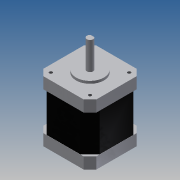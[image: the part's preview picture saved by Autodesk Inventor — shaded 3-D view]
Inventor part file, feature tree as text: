
AUTODESK INVENTOR PART (.ipt)
format: ipt  version: 2013 (Build 170138000, 138)  size: 163,840 bytes
history: native  units: mm
features: sketch x7, extrude x6, projected_geometry x3, pattern_circular x2, hole x1, chamfer x1
ambient origin geometry x8: Origin, YZ Plane, XZ Plane, XY Plane, X Axis, Y Axis, Z Axis, Center Point
bodies: Solid1 (feature_tree)
feature tree (20):
  extrude  "Extrusion1"  Depth=48.0mm TaperAngle=0.0deg
  extrude  "Extrusion2"  Depth=2.0mm TaperAngle=0.0deg
  extrude  "Extrusion3"  Depth=22.0mm TaperAngle=0.0deg
  extrude  "Extrusion4"  Depth=15.0mm TaperAngle=0.0deg
  hole  "Hole1"  [1 undecoded]
  chamfer  "Chamfer1"  Distance=30.0mm
  extrude  "Extrusion5"  Depth=40.0mm TaperAngle=360.0deg
  pattern_circular  "Circular Pattern1"  [2 undecoded]
  extrude  "Extrusion6"  Depth=40.0mm TaperAngle=360.0deg
  pattern_circular  "Circular Pattern2"  [2 undecoded]
  sketch  "Sketch1"  dims[d0=42.0mm d1=48.0mm d2=0.0mm]
  sketch  "Sketch2"  dims[d3=22.0mm d5=2.0mm d6=0.0mm]
  sketch  "Sketch3"  dims[d7=5.0mm d9=22.0mm d10=0.0mm]
  sketch  "Sketch4"  dims[d11=2.0mm d12=15.0mm d13=0.0mm]
  sketch  "Sketch5"  dims[d14=31.0mm]
  sketch  "Sketch6"  dims[d15=2.459mm d16=48.0mm d17=4.0mm d18=2.0mm d19=90.0deg d20=8.0mm d21=20.594885mm d22=5.0mm d23=2.0mm d24=45.0deg]
  sketch  "Sketch7"  dims[d25=2.0mm d26=30.0mm d27=0.0mm d28=40.0mm d29=360.0deg d31=0.1mm d32=0.0mm d33=40.0mm d34=360.0deg]
  projected_geometry  "Projected Loop1"
  projected_geometry  "Projected Loop2"
  projected_geometry  "Project Cut Edges1"
note: 5 required parameter values undecoded (feature->parameter linkage not recoverable at this tier; creation-order binding heuristic only, values carry confidence <= 0.55)
